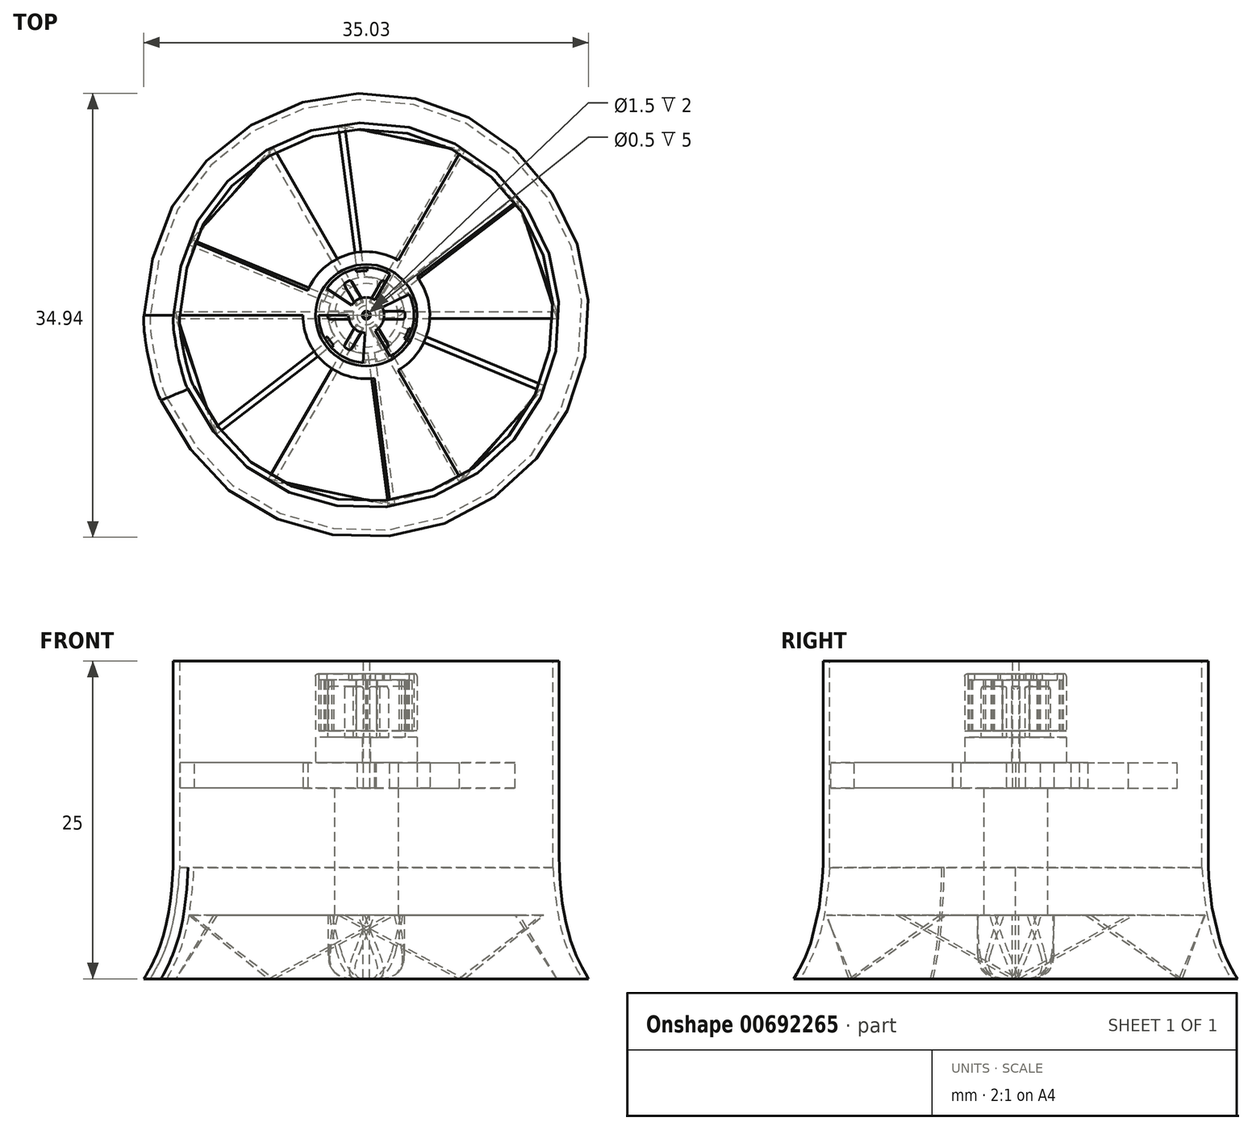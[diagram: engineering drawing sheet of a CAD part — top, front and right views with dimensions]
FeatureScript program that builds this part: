
annotation { "Feature Type Name" : "Feature", "Feature Type Description" : "" }
export const myFeature = defineFeature(function(context is Context, id is Id, definition is map)
    precondition{}
    {
        {
            var Q0;
            Q0=qCreatedBy(makeId("Top.planeOp"),FACE);
            var sketch = newSketch(context, id + "F0", { "sketchPlane" : qUnion([Q0])});
            skCircle(sketch, "E0", {"center": v(0, 0) * mm, "radius": 17.5 * mm});
            skCircle(sketch, "E1", {"center": v(0, 0) * mm, "radius": 15 * mm});
            skCircle(sketch, "E2", {"center": v(0, 0) * mm, "radius": 14.25 * mm});
            skCircle(sketch, "E3", {"center": v(0, 0) * mm, "radius": 0.5 * mm});
            skSolve(sketch);
        }
        {
            var Q0;
            Q0=qCreatedBy(makeId("Right.planeOp"),FACE);
            var sketch = newSketch(context, id + "F1", { "sketchPlane" : qUnion([Q0])});
            skFitSpline(sketch, "E4", {"points": [v(-17.47, 0) * mm, v(-16.4, 2.05) * mm, v(-15.16, 8.76) * mm], "startDerivative": vector(0.8, 0.84) * mm, "endDerivative": vector(0.72, 13.83) * mm});
            skLineSegment(sketch, "E5", {"start": v(-17.47, 0) * mm, "end": v(-16.97, 0) * mm});
            skLineSegment(sketch, "E6", {"start": v(0, 0) * mm, "end": v(0, 25) * mm});
            skLineSegment(sketch, "E7", {"start": v(-15.16, 8.76) * mm, "end": v(-15.16, 25) * mm});
            skLineSegment(sketch, "E8", {"start": v(-15.16, 25) * mm, "end": v(-14.66, 25) * mm});
            skLineSegment(sketch, "E9", {"start": v(-14.66, 25) * mm, "end": v(-14.66, 8.76) * mm});
            skLineSegment(sketch, "E10", {"start": v(-16.97, 0) * mm, "end": v(-17.47, 0) * mm});
            skFitSpline(sketch, "E11", {"points": [v(-16.97, 0) * mm, v(-15.9, 2.07) * mm, v(-14.66, 8.76) * mm], "startDerivative": vector(0.48, 0.72) * mm, "endDerivative": vector(0.94, 13.86) * mm});
            skLineSegment(sketch, "E12.MirrorCS", {"start": v(14.66, 25) * mm, "end": v(14.66, 8.76) * mm});
            skLineSegment(sketch, "E13.MirrorCS", {"start": v(15.16, 8.76) * mm, "end": v(15.16, 25) * mm});
            skLineSegment(sketch, "E14.MirrorCS", {"start": v(15.16, 25) * mm, "end": v(14.66, 25) * mm});
            skFitSpline(sketch, "E15.MirrorCS", {"points": [v(17.47, 0) * mm, v(16.4, 2.05) * mm, v(15.16, 8.76) * mm], "startDerivative": vector(-0.8, 0.84) * mm, "endDerivative": vector(-0.72, 13.83) * mm});
            skFitSpline(sketch, "E16.MirrorCS", {"points": [v(16.97, 0) * mm, v(15.9, 2.07) * mm, v(14.66, 8.76) * mm], "startDerivative": vector(-0.48, 0.72) * mm, "endDerivative": vector(-0.94, 13.86) * mm});
            skLineSegment(sketch, "E17.MirrorCS", {"start": v(16.97, 0) * mm, "end": v(17.47, 0) * mm});
            skSolve(sketch);
        }
        {
            var Q0;
            Q0=qCreatedBy(makeId("Front.planeOp"),FACE);
            var sketch = newSketch(context, id + "F2", { "sketchPlane" : qUnion([Q0])});
            skFitSpline(sketch, "E18", {"points": [v(-17.5, 0) * mm, v(-16.43, 2.05) * mm, v(-15.18, 8.76) * mm], "startDerivative": vector(0.8, 0.84) * mm, "endDerivative": vector(0.72, 13.83) * mm});
            skLineSegment(sketch, "E19", {"start": v(-15.18, 8.76) * mm, "end": v(-15.18, 25) * mm});
            skLineSegment(sketch, "E20", {"start": v(-15.18, 25) * mm, "end": v(-14.68, 25) * mm});
            skLineSegment(sketch, "E21", {"start": v(-14.68, 25) * mm, "end": v(-14.68, 8.76) * mm});
            skLineSegment(sketch, "E22", {"start": v(-17, 0) * mm, "end": v(-17.5, 0) * mm});
            skFitSpline(sketch, "E23", {"points": [v(-17, 0) * mm, v(-15.93, 2.07) * mm, v(-14.68, 8.76) * mm], "startDerivative": vector(0.48, 0.72) * mm, "endDerivative": vector(0.94, 13.86) * mm});
            skLineSegment(sketch, "E24.MirrorCS", {"start": v(14.68, 25) * mm, "end": v(14.68, 8.76) * mm});
            skLineSegment(sketch, "E25.MirrorCS", {"start": v(15.18, 8.76) * mm, "end": v(15.18, 25) * mm});
            skLineSegment(sketch, "E26.MirrorCS", {"start": v(15.18, 25) * mm, "end": v(14.68, 25) * mm});
            skFitSpline(sketch, "E27.MirrorCS", {"points": [v(17, 0) * mm, v(15.93, 2.07) * mm, v(14.68, 8.76) * mm], "startDerivative": vector(-0.48, 0.72) * mm, "endDerivative": vector(-0.94, 13.86) * mm});
            skFitSpline(sketch, "E28.MirrorCS", {"points": [v(17.5, 0) * mm, v(16.43, 2.05) * mm, v(15.18, 8.76) * mm], "startDerivative": vector(-0.8, 0.84) * mm, "endDerivative": vector(-0.72, 13.83) * mm});
            skLineSegment(sketch, "E29.MirrorCS", {"start": v(17, 0) * mm, "end": v(17.5, 0) * mm});
            skSolve(sketch);
        }
        {
            var Q0;
            Q0=qCreatedBy(makeId("Right.planeOp"),FACE);
            var Q1;
            Q1=qCreatedBy(makeId("Front.planeOp"),FACE);
            cPlane(context, id + "F3", {"entities" : qUnion([Q0, Q1]), "cplaneType" : CPlaneType.MID_PLANE, "offset" : 25 * mm, "width" : 150 * mm, "height" : 150 * mm});
        }
        {
            var Q0;
            Q0=qCreatedBy(makeId("Right.planeOp"),FACE);
            var Q1;
            Q1=qCreatedBy(makeId("Front.planeOp"),FACE);
            cPlane(context, id + "F4", {"entities" : qUnion([Q0, Q1]), "cplaneType" : CPlaneType.MID_PLANE, "offset" : 25 * mm, "flipAlignment" : true, "width" : 150 * mm, "height" : 150 * mm});
        }
        {
            var Q0;
            Q0=qCreatedBy(id+"F3.planeOp",FACE);
            var Q1;
            Q1=qCreatedBy(makeId("Right.planeOp"),FACE);
            cPlane(context, id + "F5", {"entities" : qUnion([Q0, Q1]), "cplaneType" : CPlaneType.MID_PLANE, "offset" : 25 * mm, "width" : 150 * mm, "height" : 150 * mm});
        }
        {
            var Q0;
            Q0=qCreatedBy(id+"F3.planeOp",FACE);
            var Q1;
            Q1=qCreatedBy(makeId("Right.planeOp"),FACE);
            cPlane(context, id + "F6", {"entities" : qUnion([Q0, Q1]), "cplaneType" : CPlaneType.MID_PLANE, "offset" : 25 * mm, "flipAlignment" : true, "width" : 150 * mm, "height" : 150 * mm});
        }
        {
            var Q0;
            Q0=qCreatedBy(makeId("Right.planeOp"),FACE);
            var Q1;
            Q1=qCreatedBy(id+"F4.planeOp",FACE);
            cPlane(context, id + "F7", {"entities" : qUnion([Q0, Q1]), "cplaneType" : CPlaneType.MID_PLANE, "offset" : 25 * mm, "width" : 150 * mm, "height" : 150 * mm});
        }
        {
            var Q0;
            Q0=qCreatedBy(makeId("Right.planeOp"),FACE);
            var Q1;
            Q1=qCreatedBy(id+"F4.planeOp",FACE);
            cPlane(context, id + "F8", {"entities" : qUnion([Q0, Q1]), "cplaneType" : CPlaneType.MID_PLANE, "offset" : 25 * mm, "flipAlignment" : true, "width" : 150 * mm, "height" : 150 * mm});
        }
        {
            var Q0;
            Q0=qCreatedBy(id+"F3.planeOp",FACE);
            var sketch = newSketch(context, id + "F9", { "sketchPlane" : qUnion([Q0])});
            skFitSpline(sketch, "E30", {"points": [v(-17.5, 0) * mm, v(-16.43, 2.05) * mm, v(-15.18, 8.76) * mm], "startDerivative": vector(0.8, 0.84) * mm, "endDerivative": vector(0.72, 13.83) * mm});
            skLineSegment(sketch, "E31", {"start": v(-15.18, 8.76) * mm, "end": v(-15.18, 25) * mm});
            skLineSegment(sketch, "E32", {"start": v(-15.18, 25) * mm, "end": v(-14.68, 25) * mm});
            skLineSegment(sketch, "E33", {"start": v(-14.68, 25) * mm, "end": v(-14.68, 8.76) * mm});
            skLineSegment(sketch, "E34", {"start": v(-17, 0) * mm, "end": v(-17.5, 0) * mm});
            skFitSpline(sketch, "E35", {"points": [v(-17, 0) * mm, v(-15.93, 2.07) * mm, v(-14.68, 8.76) * mm], "startDerivative": vector(0.48, 0.72) * mm, "endDerivative": vector(0.94, 13.86) * mm});
            skLineSegment(sketch, "E36.MirrorCS", {"start": v(14.68, 25) * mm, "end": v(14.68, 8.76) * mm});
            skLineSegment(sketch, "E37.MirrorCS", {"start": v(15.18, 8.76) * mm, "end": v(15.18, 25) * mm});
            skFitSpline(sketch, "E38.MirrorCS", {"points": [v(17, 0) * mm, v(15.93, 2.07) * mm, v(14.68, 8.76) * mm], "startDerivative": vector(-0.48, 0.72) * mm, "endDerivative": vector(-0.94, 13.86) * mm});
            skFitSpline(sketch, "E39.MirrorCS", {"points": [v(17.5, 0) * mm, v(16.43, 2.05) * mm, v(15.18, 8.76) * mm], "startDerivative": vector(-0.8, 0.84) * mm, "endDerivative": vector(-0.72, 13.83) * mm});
            skLineSegment(sketch, "E40.MirrorCS", {"start": v(15.18, 25) * mm, "end": v(14.68, 25) * mm});
            skLineSegment(sketch, "E41.MirrorCS", {"start": v(17, 0) * mm, "end": v(17.5, 0) * mm});
            skSolve(sketch);
        }
        {
            var Q0;
            Q0=qCreatedBy(id+"F4.planeOp",FACE);
            var sketch = newSketch(context, id + "F10", { "sketchPlane" : qUnion([Q0])});
            skFitSpline(sketch, "E42", {"points": [v(-17.5, 0) * mm, v(-16.43, 2.05) * mm, v(-15.18, 8.76) * mm], "startDerivative": vector(0.8, 0.84) * mm, "endDerivative": vector(0.72, 13.83) * mm});
            skLineSegment(sketch, "E43", {"start": v(-15.18, 8.76) * mm, "end": v(-15.18, 25) * mm});
            skLineSegment(sketch, "E44", {"start": v(-15.18, 25) * mm, "end": v(-14.68, 25) * mm});
            skLineSegment(sketch, "E45", {"start": v(-14.68, 25) * mm, "end": v(-14.68, 8.76) * mm});
            skLineSegment(sketch, "E46", {"start": v(-17, 0) * mm, "end": v(-17.5, 0) * mm});
            skFitSpline(sketch, "E47", {"points": [v(-17, 0) * mm, v(-15.93, 2.07) * mm, v(-14.68, 8.76) * mm], "startDerivative": vector(0.48, 0.72) * mm, "endDerivative": vector(0.94, 13.86) * mm});
            skLineSegment(sketch, "E48.MirrorCS", {"start": v(14.68, 25) * mm, "end": v(14.68, 8.76) * mm});
            skLineSegment(sketch, "E49.MirrorCS", {"start": v(15.18, 8.76) * mm, "end": v(15.18, 25) * mm});
            skLineSegment(sketch, "E50.MirrorCS", {"start": v(15.18, 25) * mm, "end": v(14.68, 25) * mm});
            skFitSpline(sketch, "E51.MirrorCS", {"points": [v(17.5, 0) * mm, v(16.43, 2.05) * mm, v(15.18, 8.76) * mm], "startDerivative": vector(-0.8, 0.84) * mm, "endDerivative": vector(-0.72, 13.83) * mm});
            skFitSpline(sketch, "E52.MirrorCS", {"points": [v(17, 0) * mm, v(15.93, 2.07) * mm, v(14.68, 8.76) * mm], "startDerivative": vector(-0.48, 0.72) * mm, "endDerivative": vector(-0.94, 13.86) * mm});
            skLineSegment(sketch, "E53.MirrorCS", {"start": v(17, 0) * mm, "end": v(17.5, 0) * mm});
            skSolve(sketch);
        }
        {
            var Q0;
            Q0=qCreatedBy(id+"F5.planeOp",FACE);
            var sketch = newSketch(context, id + "F11", { "sketchPlane" : qUnion([Q0])});
            skFitSpline(sketch, "E54", {"points": [v(-17.5, 0) * mm, v(-16.43, 2.05) * mm, v(-15.18, 8.76) * mm], "startDerivative": vector(0.8, 0.84) * mm, "endDerivative": vector(0.72, 13.83) * mm});
            skLineSegment(sketch, "E55", {"start": v(-15.18, 8.76) * mm, "end": v(-15.18, 25) * mm});
            skLineSegment(sketch, "E56", {"start": v(-15.18, 25) * mm, "end": v(-14.68, 25) * mm});
            skLineSegment(sketch, "E57", {"start": v(-14.68, 25) * mm, "end": v(-14.68, 8.76) * mm});
            skLineSegment(sketch, "E58", {"start": v(-17, 0) * mm, "end": v(-17.5, 0) * mm});
            skFitSpline(sketch, "E59", {"points": [v(-17, 0) * mm, v(-15.93, 2.07) * mm, v(-14.68, 8.76) * mm], "startDerivative": vector(0.48, 0.72) * mm, "endDerivative": vector(0.94, 13.86) * mm});
            skLineSegment(sketch, "E60.MirrorCS", {"start": v(14.68, 25) * mm, "end": v(14.68, 8.76) * mm});
            skLineSegment(sketch, "E61.MirrorCS", {"start": v(15.18, 25) * mm, "end": v(14.68, 25) * mm});
            skLineSegment(sketch, "E62.MirrorCS", {"start": v(15.18, 8.76) * mm, "end": v(15.18, 25) * mm});
            skFitSpline(sketch, "E63.MirrorCS", {"points": [v(17, 0) * mm, v(15.93, 2.07) * mm, v(14.68, 8.76) * mm], "startDerivative": vector(-0.48, 0.72) * mm, "endDerivative": vector(-0.94, 13.86) * mm});
            skFitSpline(sketch, "E64.MirrorCS", {"points": [v(17.5, 0) * mm, v(16.43, 2.05) * mm, v(15.18, 8.76) * mm], "startDerivative": vector(-0.8, 0.84) * mm, "endDerivative": vector(-0.72, 13.83) * mm});
            skLineSegment(sketch, "E65.MirrorCS", {"start": v(17, 0) * mm, "end": v(17.5, 0) * mm});
            skSolve(sketch);
        }
        {
            var Q0;
            Q0=qCreatedBy(id+"F6.planeOp",FACE);
            var sketch = newSketch(context, id + "F12", { "sketchPlane" : qUnion([Q0])});
            skFitSpline(sketch, "E66", {"points": [v(-17.5, 0) * mm, v(-16.43, 2.05) * mm, v(-15.18, 8.76) * mm], "startDerivative": vector(0.8, 0.84) * mm, "endDerivative": vector(0.72, 13.83) * mm});
            skLineSegment(sketch, "E67", {"start": v(-15.18, 8.76) * mm, "end": v(-15.18, 25) * mm});
            skLineSegment(sketch, "E68", {"start": v(-15.18, 25) * mm, "end": v(-14.68, 25) * mm});
            skLineSegment(sketch, "E69", {"start": v(-14.68, 25) * mm, "end": v(-14.68, 8.76) * mm});
            skLineSegment(sketch, "E70", {"start": v(-17, 0) * mm, "end": v(-17.5, 0) * mm});
            skFitSpline(sketch, "E71", {"points": [v(-17, 0) * mm, v(-15.93, 2.07) * mm, v(-14.68, 8.76) * mm], "startDerivative": vector(0.48, 0.72) * mm, "endDerivative": vector(0.94, 13.86) * mm});
            skLineSegment(sketch, "E72.MirrorCS", {"start": v(14.68, 25) * mm, "end": v(14.68, 8.76) * mm});
            skLineSegment(sketch, "E73.MirrorCS", {"start": v(15.18, 8.76) * mm, "end": v(15.18, 25) * mm});
            skFitSpline(sketch, "E74.MirrorCS", {"points": [v(17, 0) * mm, v(15.93, 2.07) * mm, v(14.68, 8.76) * mm], "startDerivative": vector(-0.48, 0.72) * mm, "endDerivative": vector(-0.94, 13.86) * mm});
            skFitSpline(sketch, "E75.MirrorCS", {"points": [v(17.5, 0) * mm, v(16.43, 2.05) * mm, v(15.18, 8.76) * mm], "startDerivative": vector(-0.8, 0.84) * mm, "endDerivative": vector(-0.72, 13.83) * mm});
            skLineSegment(sketch, "E76.MirrorCS", {"start": v(15.18, 25) * mm, "end": v(14.68, 25) * mm});
            skLineSegment(sketch, "E77.MirrorCS", {"start": v(17, 0) * mm, "end": v(17.5, 0) * mm});
            skSolve(sketch);
        }
        {
            var Q0;
            Q0=qCreatedBy(id+"F7.planeOp",FACE);
            var sketch = newSketch(context, id + "F13", { "sketchPlane" : qUnion([Q0])});
            skFitSpline(sketch, "E78", {"points": [v(-17.5, 0) * mm, v(-16.43, 2.05) * mm, v(-15.18, 8.76) * mm], "startDerivative": vector(0.8, 0.84) * mm, "endDerivative": vector(0.72, 13.83) * mm});
            skLineSegment(sketch, "E79", {"start": v(-15.18, 8.76) * mm, "end": v(-15.18, 25) * mm});
            skLineSegment(sketch, "E80", {"start": v(-15.18, 25) * mm, "end": v(-14.68, 25) * mm});
            skLineSegment(sketch, "E81", {"start": v(-14.68, 25) * mm, "end": v(-14.68, 8.76) * mm});
            skLineSegment(sketch, "E82", {"start": v(-17, 0) * mm, "end": v(-17.5, 0) * mm});
            skFitSpline(sketch, "E83", {"points": [v(-17, 0) * mm, v(-15.93, 2.07) * mm, v(-14.68, 8.76) * mm], "startDerivative": vector(0.48, 0.72) * mm, "endDerivative": vector(0.94, 13.86) * mm});
            skLineSegment(sketch, "E84.MirrorCS", {"start": v(14.68, 25) * mm, "end": v(14.68, 8.76) * mm});
            skLineSegment(sketch, "E85.MirrorCS", {"start": v(15.18, 8.76) * mm, "end": v(15.18, 25) * mm});
            skFitSpline(sketch, "E86.MirrorCS", {"points": [v(17, 0) * mm, v(15.93, 2.07) * mm, v(14.68, 8.76) * mm], "startDerivative": vector(-0.48, 0.72) * mm, "endDerivative": vector(-0.94, 13.86) * mm});
            skFitSpline(sketch, "E87.MirrorCS", {"points": [v(17.5, 0) * mm, v(16.43, 2.05) * mm, v(15.18, 8.76) * mm], "startDerivative": vector(-0.8, 0.84) * mm, "endDerivative": vector(-0.72, 13.83) * mm});
            skLineSegment(sketch, "E88.MirrorCS", {"start": v(15.18, 25) * mm, "end": v(14.68, 25) * mm});
            skLineSegment(sketch, "E89.MirrorCS", {"start": v(17, 0) * mm, "end": v(17.5, 0) * mm});
            skSolve(sketch);
        }
        {
            var Q0;
            Q0=qCreatedBy(id+"F8.planeOp",FACE);
            var sketch = newSketch(context, id + "F14", { "sketchPlane" : qUnion([Q0])});
            skFitSpline(sketch, "E90", {"points": [v(-17.5, 0) * mm, v(-16.43, 2.05) * mm, v(-15.18, 8.76) * mm], "startDerivative": vector(0.8, 0.84) * mm, "endDerivative": vector(0.72, 13.83) * mm});
            skLineSegment(sketch, "E91", {"start": v(-15.18, 8.76) * mm, "end": v(-15.18, 25) * mm});
            skLineSegment(sketch, "E92", {"start": v(-15.18, 25) * mm, "end": v(-14.68, 25) * mm});
            skLineSegment(sketch, "E93", {"start": v(-14.68, 25) * mm, "end": v(-14.68, 8.76) * mm});
            skLineSegment(sketch, "E94", {"start": v(-17, 0) * mm, "end": v(-17.5, 0) * mm});
            skFitSpline(sketch, "E95", {"points": [v(-17, 0) * mm, v(-15.93, 2.07) * mm, v(-14.68, 8.76) * mm], "startDerivative": vector(0.48, 0.72) * mm, "endDerivative": vector(0.94, 13.86) * mm});
            skLineSegment(sketch, "E96.MirrorCS", {"start": v(14.68, 25) * mm, "end": v(14.68, 8.76) * mm});
            skLineSegment(sketch, "E97.MirrorCS", {"start": v(15.18, 8.76) * mm, "end": v(15.18, 25) * mm});
            skFitSpline(sketch, "E98.MirrorCS", {"points": [v(17.5, 0) * mm, v(16.43, 2.05) * mm, v(15.18, 8.76) * mm], "startDerivative": vector(-0.8, 0.84) * mm, "endDerivative": vector(-0.72, 13.83) * mm});
            skFitSpline(sketch, "E99.MirrorCS", {"points": [v(17, 0) * mm, v(15.93, 2.07) * mm, v(14.68, 8.76) * mm], "startDerivative": vector(-0.48, 0.72) * mm, "endDerivative": vector(-0.94, 13.86) * mm});
            skLineSegment(sketch, "E100.MirrorCS", {"start": v(17, 0) * mm, "end": v(17.5, 0) * mm});
            skLineSegment(sketch, "E101.MirrorCS", {"start": v(15.18, 25) * mm, "end": v(14.68, 25) * mm});
            skSolve(sketch);
        }
        {
            var Q0;
            Q0=makeQuery(id+"F11.imprint","IMPRINT",FACE,{"disambiguationData":[TD([[makeQuery(id+"F11.imprint","IMPRINT",EDGE,{"derivedFrom":sQuery(id+"F11.wireOp",EDGE,"E60.MirrorCS")}),1.0]])]});
            var Q1;
            Q1=makeQuery(id+"F10.imprint","IMPRINT",FACE,{"disambiguationData":[TD([[makeQuery(id+"F10.imprint","IMPRINT",EDGE,{"derivedFrom":sQuery(id+"F10.wireOp",EDGE,"E42")}),-1.0]])]});
            var Q2;
            Q2=makeQuery(id+"F14.imprint","IMPRINT",FACE,{"disambiguationData":[TD([[makeQuery(id+"F14.imprint","IMPRINT",EDGE,{"derivedFrom":sQuery(id+"F14.wireOp",EDGE,"E90")}),-1.0]])]});
            var Q3;
            Q3=makeQuery(id+"F1.imprint","IMPRINT",FACE,{"disambiguationData":[TD([[makeQuery(id+"F1.imprint","IMPRINT",EDGE,{"derivedFrom":sQuery(id+"F1.wireOp",EDGE,"E4")}),-1.0]])]});
            var Q4;
            Q4=makeQuery(id+"F12.imprint","IMPRINT",FACE,{"disambiguationData":[TD([[makeQuery(id+"F12.imprint","IMPRINT",EDGE,{"derivedFrom":sQuery(id+"F12.wireOp",EDGE,"E66")}),-1.0]])]});
            var Q5;
            Q5=makeQuery(id+"F9.imprint","IMPRINT",FACE,{"disambiguationData":[TD([[makeQuery(id+"F9.imprint","IMPRINT",EDGE,{"derivedFrom":sQuery(id+"F9.wireOp",EDGE,"E30")}),-1.0]])]});
            var Q6;
            Q6=makeQuery(id+"F13.imprint","IMPRINT",FACE,{"disambiguationData":[TD([[makeQuery(id+"F13.imprint","IMPRINT",EDGE,{"derivedFrom":sQuery(id+"F13.wireOp",EDGE,"E78")}),-1.0]])]});
            var Q7;
            Q7=makeQuery(id+"F2.imprint","IMPRINT",FACE,{"disambiguationData":[TD([[makeQuery(id+"F2.imprint","IMPRINT",EDGE,{"derivedFrom":sQuery(id+"F2.wireOp",EDGE,"E24.MirrorCS")}),1.0]])]});
            var Q8;
            Q8=makeQuery(id+"F11.imprint","IMPRINT",FACE,{"disambiguationData":[TD([[makeQuery(id+"F11.imprint","IMPRINT",EDGE,{"derivedFrom":sQuery(id+"F11.wireOp",EDGE,"E54")}),-1.0]])]});
            var Q9;
            Q9=makeQuery(id+"F10.imprint","IMPRINT",FACE,{"disambiguationData":[TD([[makeQuery(id+"F10.imprint","IMPRINT",EDGE,{"derivedFrom":sQuery(id+"F10.wireOp",EDGE,"E48.MirrorCS")}),1.0]])]});
            var Q10;
            Q10=makeQuery(id+"F14.imprint","IMPRINT",FACE,{"disambiguationData":[TD([[makeQuery(id+"F14.imprint","IMPRINT",EDGE,{"derivedFrom":sQuery(id+"F14.wireOp",EDGE,"E96.MirrorCS")}),1.0]])]});
            var Q11;
            Q11=makeQuery(id+"F1.imprint","IMPRINT",FACE,{"disambiguationData":[TD([[makeQuery(id+"F1.imprint","IMPRINT",EDGE,{"derivedFrom":sQuery(id+"F1.wireOp",EDGE,"E12.MirrorCS")}),1.0]])]});
            var Q12;
            Q12=makeQuery(id+"F12.imprint","IMPRINT",FACE,{"disambiguationData":[TD([[makeQuery(id+"F12.imprint","IMPRINT",EDGE,{"derivedFrom":sQuery(id+"F12.wireOp",EDGE,"E72.MirrorCS")}),1.0]])]});
            var Q13;
            Q13=makeQuery(id+"F9.imprint","IMPRINT",FACE,{"disambiguationData":[TD([[makeQuery(id+"F9.imprint","IMPRINT",EDGE,{"derivedFrom":sQuery(id+"F9.wireOp",EDGE,"E36.MirrorCS")}),1.0]])]});
            var Q14;
            Q14=makeQuery(id+"F13.imprint","IMPRINT",FACE,{"disambiguationData":[TD([[makeQuery(id+"F13.imprint","IMPRINT",EDGE,{"derivedFrom":sQuery(id+"F13.wireOp",EDGE,"E84.MirrorCS")}),1.0]])]});
            var Q15;
            Q15=makeQuery(id+"F2.imprint","IMPRINT",FACE,{"disambiguationData":[TD([[makeQuery(id+"F2.imprint","IMPRINT",EDGE,{"derivedFrom":sQuery(id+"F2.wireOp",EDGE,"E18")}),-1.0]])]});
            loft(context, id + "F15", {"sheetProfilesArray" : [{ "sheetProfileEntities" : qUnion([Q0]) }, { "sheetProfileEntities" : qUnion([Q1]) }, { "sheetProfileEntities" : qUnion([Q2]) }, { "sheetProfileEntities" : qUnion([Q3]) }, { "sheetProfileEntities" : qUnion([Q4]) }, { "sheetProfileEntities" : qUnion([Q5]) }, { "sheetProfileEntities" : qUnion([Q6]) }, { "sheetProfileEntities" : qUnion([Q7]) }, { "sheetProfileEntities" : qUnion([Q8]) }, { "sheetProfileEntities" : qUnion([Q9]) }, { "sheetProfileEntities" : qUnion([Q10]) }, { "sheetProfileEntities" : qUnion([Q11]) }, { "sheetProfileEntities" : qUnion([Q12]) }, { "sheetProfileEntities" : qUnion([Q13]) }, { "sheetProfileEntities" : qUnion([Q14]) }, { "sheetProfileEntities" : qUnion([Q15]) }]});
        }
        {
            var Q1;
            Q1=makeQuery(id+"F15.opLoft","CAP_FACE",FACE,{"disambiguationData":[OSD([makeQuery(id+"F2.imprint","IMPRINT",FACE,{"disambiguationData":[TD([[makeQuery(id+"F2.imprint","IMPRINT",EDGE,{"derivedFrom":sQuery(id+"F2.wireOp",EDGE,"E18")}),-1.0]])]})])],"isStart":true});
            var Q2;
            Q2=makeQuery(id+"F15.opLoft","CAP_FACE",FACE,{"disambiguationData":[OSD([makeQuery(id+"F11.imprint","IMPRINT",FACE,{"disambiguationData":[TD([[makeQuery(id+"F11.imprint","IMPRINT",EDGE,{"derivedFrom":sQuery(id+"F11.wireOp",EDGE,"E60.MirrorCS")}),1.0]])]})])],"isStart":true});
            loft(context, id + "F16", {"operationType" : NewBodyOperationType.ADD, "startCondition" : LoftEndDerivativeType.MATCH_CURVATURE, "startMagnitude" : 0.5, "endCondition" : LoftEndDerivativeType.MATCH_CURVATURE, "endMagnitude" : 0.5, "sheetProfilesArray" : [{ "sheetProfileEntities" : qUnion([Q1]) }, { "sheetProfileEntities" : qUnion([Q2]) }]});
        }
        {
            var Q0;
            Q0=qCreatedBy(makeId("Top.planeOp"),FACE);
            cPlane(context, id + "F17", {"entities" : qUnion([Q0]), "cplaneType" : CPlaneType.OFFSET, "offset" : 15 * mm, "width" : 150 * mm, "height" : 150 * mm});
        }
        {
            var Q0;
            Q0=qCreatedBy(id+"F17.planeOp",FACE);
            var sketch = newSketch(context, id + "F18", { "sketchPlane" : qUnion([Q0])});
            skCircle(sketch, "E102", {"center": v(0, 0) * mm, "radius": 5 * mm});
            skArc(sketch, "E103", {"start": v(-13.6, 5.72) * mm, "mid": v(-14.46, 2.92) * mm, "end": v(-14.75, 0) * mm});
            skLineSegment(sketch, "E104", {"start": v(-5, 0) * mm, "end": v(-14.75, 0) * mm});
            skLineSegment(sketch, "E105", {"start": v(-4.6, 1.94) * mm, "end": v(-13.6, 5.72) * mm});
            skLineSegment(sketch, "E106.1.0", {"start": v(2.5, -4.33) * mm, "end": v(7.38, -12.77) * mm});
            skLineSegment(sketch, "E106.1.1", {"start": v(0.62, -4.96) * mm, "end": v(1.84, -14.63) * mm});
            skArc(sketch, "E106.1.2", {"start": v(1.84, -14.63) * mm, "mid": v(4.7, -13.98) * mm, "end": v(7.37, -12.77) * mm});
            skLineSegment(sketch, "E106.2.0", {"start": v(2.5, 4.33) * mm, "end": v(7.38, 12.77) * mm});
            skLineSegment(sketch, "E106.2.1", {"start": v(3.98, 3.02) * mm, "end": v(11.75, 8.91) * mm});
            skArc(sketch, "E106.2.2", {"start": v(11.75, 8.91) * mm, "mid": v(9.76, 11.06) * mm, "end": v(7.38, 12.77) * mm});
            skCircle(sketch, "E107", {"center": v(0, 0) * mm, "radius": 0.75 * mm});
            skSolve(sketch);
        }
        {
            var Q0;
            {var subQ0=sQuery(id+"F18.wireOp",EDGE,"E106.2.0");Q0=makeQuery(id+"F18.imprint","IMPRINT",FACE,{"disambiguationData":[TD([[makeQuery(id+"F18.imprint","IMPRINT",EDGE,{"derivedFrom":subQ0}),-1.0]])]});}
            var Q1;
            Q1=makeQuery(id+"F18.imprint","IMPRINT",FACE,{"disambiguationData":[TD([[makeQuery(id+"F18.imprint","IMPRINT",EDGE,{"derivedFrom":sQuery(id+"F18.wireOp",EDGE,"E103")}),1.0]])]});
            var Q2;
            {var subQ0=sQuery(id+"F18.wireOp",EDGE,"E102");var subQ4=makeQuery(id+"F18.imprint","INTERSECT",VERTEX,{"derivedFrom":[subQ0,sQuery(id+"F18.wireOp",EDGE,"E106.2.0")]});Q2=makeQuery(id+"F18.imprint","IMPRINT",FACE,{"disambiguationData":[TD([[makeQuery(id+"F18.imprint","IMPRINT",EDGE,{"disambiguationData":[TD([[subQ4,1.0]])],"derivedFrom":subQ0}),1.0]])]});}
            var Q3;
            {var subQ0=sQuery(id+"F18.wireOp",EDGE,"E106.1.0");Q3=makeQuery(id+"F18.imprint","IMPRINT",FACE,{"disambiguationData":[TD([[makeQuery(id+"F18.imprint","IMPRINT",EDGE,{"derivedFrom":subQ0}),-1.0]])]});}
            extrude(context, id + "F19", {"entities" : qUnion([Q0, Q1, Q2, Q3]), "operationType" : NewBodyOperationType.ADD, "depth" : 2 * mm, "offsetDistance" : 25 * mm});
        }
        {
            var Q0;
            Q0=qCreatedBy(makeId("Top.planeOp"),FACE);
            cPlane(context, id + "F20", {"entities" : qUnion([Q0]), "cplaneType" : CPlaneType.OFFSET, "offset" : 5 * mm, "width" : 150 * mm, "height" : 150 * mm});
        }
        {
            var Q0;
            Q0=qCreatedBy(id+"F20.planeOp",FACE);
            var sketch = newSketch(context, id + "F21", { "sketchPlane" : qUnion([Q0])});
            skCircle(sketch, "E108", {"center": v(0, 0) * mm, "radius": 3 * mm});
            skCircle(sketch, "E109", {"center": v(0, 0) * mm, "radius": 15 * mm});
            skCircle(sketch, "E110", {"center": v(0, 0) * mm, "radius": 0.25 * mm});
            skSolve(sketch);
        }
        {
            var Q0;
            Q0=makeQuery(id+"F21.imprint","IMPRINT",FACE,{"disambiguationData":[TD([[makeQuery(id+"F21.imprint","IMPRINT",EDGE,{"derivedFrom":sQuery(id+"F21.wireOp",EDGE,"E108")}),1.0]])]});
            extrude(context, id + "F22", {"entities" : qUnion([Q0]), "oppositeDirection" : true, "depth" : 5 * mm, "offsetDistance" : 25 * mm});
        }
        {
            var Q0;
            Q0=makeQuery(id+"F22.opExtrude","CAP_EDGE",EDGE,{"disambiguationData":[OSD([sQuery(id+"F21.wireOp",EDGE,"E108")])],"isStart":false});
            fillet(context, id + "F23", {"entities" : qUnion([Q0]), "radius" : 2 * mm, "rho" : 0.5, "crossSection" : FilletCrossSection.CONIC, "allowEdgeOverflow" : false});
        }
        {
            var Q0;
            Q0=qCreatedBy(makeId("Top.planeOp"),FACE);
            var sketch = newSketch(context, id + "F24", { "sketchPlane" : qUnion([Q0])});
            skLineSegment(sketch, "E111", {"start": v(0, 0.25) * mm, "end": v(0, -0.25) * mm});
            skLineSegment(sketch, "E112", {"start": v(-0.43, 0.25) * mm, "end": v(-15, 0.25) * mm});
            skLineSegment(sketch, "E113", {"start": v(-15, 0.25) * mm, "end": v(-15, -0.25) * mm});
            skLineSegment(sketch, "E114", {"start": v(-15, -0.25) * mm, "end": v(-0.43, -0.25) * mm});
            skArc(sketch, "E115", {"start": v(-0.43, 0.25) * mm, "mid": v(-0.5, 0) * mm, "end": v(-0.43, -0.25) * mm});
            skLineSegment(sketch, "E116.1.0", {"start": v(-7.72, -12.87) * mm, "end": v(-7.28, -13.12) * mm});
            skLineSegment(sketch, "E116.1.1", {"start": v(-0.43, -0.25) * mm, "end": v(-7.72, -12.87) * mm});
            skLineSegment(sketch, "E116.1.2", {"start": v(-7.28, -13.12) * mm, "end": v(0, -0.5) * mm});
            skArc(sketch, "E116.1.3", {"start": v(-0.43, -0.25) * mm, "mid": v(-0.25, -0.43) * mm, "end": v(0, -0.5) * mm});
            skLineSegment(sketch, "E116.2.0", {"start": v(7.28, -13.12) * mm, "end": v(7.72, -12.87) * mm});
            skLineSegment(sketch, "E116.2.1", {"start": v(0, -0.5) * mm, "end": v(7.28, -13.12) * mm});
            skLineSegment(sketch, "E116.2.2", {"start": v(7.72, -12.87) * mm, "end": v(0.43, -0.25) * mm});
            skArc(sketch, "E116.2.3", {"start": v(0, -0.5) * mm, "mid": v(0.25, -0.43) * mm, "end": v(0.43, -0.25) * mm});
            skLineSegment(sketch, "E116.3.0", {"start": v(15, -0.25) * mm, "end": v(15, 0.25) * mm});
            skLineSegment(sketch, "E116.3.1", {"start": v(0.43, -0.25) * mm, "end": v(15, -0.25) * mm});
            skLineSegment(sketch, "E116.3.2", {"start": v(15, 0.25) * mm, "end": v(0.43, 0.25) * mm});
            skArc(sketch, "E116.3.3", {"start": v(0.43, -0.25) * mm, "mid": v(0.5, 0) * mm, "end": v(0.43, 0.25) * mm});
            skLineSegment(sketch, "E116.4.0", {"start": v(7.72, 12.87) * mm, "end": v(7.28, 13.12) * mm});
            skLineSegment(sketch, "E116.4.1", {"start": v(0.43, 0.25) * mm, "end": v(7.72, 12.87) * mm});
            skLineSegment(sketch, "E116.4.2", {"start": v(7.28, 13.12) * mm, "end": v(0, 0.5) * mm});
            skArc(sketch, "E116.4.3", {"start": v(0.43, 0.25) * mm, "mid": v(0.25, 0.43) * mm, "end": v(0, 0.5) * mm});
            skLineSegment(sketch, "E116.5.0", {"start": v(-7.28, 13.12) * mm, "end": v(-7.72, 12.87) * mm});
            skLineSegment(sketch, "E116.5.1", {"start": v(0, 0.5) * mm, "end": v(-7.28, 13.12) * mm});
            skLineSegment(sketch, "E116.5.2", {"start": v(-7.72, 12.87) * mm, "end": v(-0.43, 0.25) * mm});
            skArc(sketch, "E116.5.3", {"start": v(0, 0.5) * mm, "mid": v(-0.25, 0.43) * mm, "end": v(-0.43, 0.25) * mm});
            skSolve(sketch);
        }
        {
            var Q0;
            Q0=qCreatedBy(id+"F20.planeOp",FACE);
            var sketch = newSketch(context, id + "F25", { "sketchPlane" : qUnion([Q0])});
            skLineSegment(sketch, "E117", {"start": v(-0.5, -0.07) * mm, "end": v(-13.95, 5.5) * mm});
            skLineSegment(sketch, "E118", {"start": v(-13.95, 5.5) * mm, "end": v(-13.76, 5.97) * mm});
            skLineSegment(sketch, "E119", {"start": v(-13.76, 5.97) * mm, "end": v(-0.3, 0.4) * mm});
            skArc(sketch, "E120", {"start": v(-0.3, 0.4) * mm, "mid": v(-0.46, 0.2) * mm, "end": v(-0.5, -0.07) * mm});
            skLineSegment(sketch, "E121.1.0", {"start": v(-12.05, -8.93) * mm, "end": v(-0.5, -0.07) * mm});
            skLineSegment(sketch, "E121.1.1", {"start": v(-0.2, -0.46) * mm, "end": v(-11.75, -9.33) * mm});
            skLineSegment(sketch, "E121.1.2", {"start": v(-11.75, -9.33) * mm, "end": v(-12.05, -8.93) * mm});
            skArc(sketch, "E121.1.3", {"start": v(-0.5, -0.07) * mm, "mid": v(-0.4, -0.3) * mm, "end": v(-0.2, -0.46) * mm});
            skLineSegment(sketch, "E121.2.0", {"start": v(1.71, -14.9) * mm, "end": v(-0.2, -0.46) * mm});
            skLineSegment(sketch, "E121.2.1", {"start": v(0.3, -0.4) * mm, "end": v(2.2, -14.84) * mm});
            skLineSegment(sketch, "E121.2.2", {"start": v(2.2, -14.84) * mm, "end": v(1.71, -14.9) * mm});
            skArc(sketch, "E121.2.3", {"start": v(-0.2, -0.46) * mm, "mid": v(0.07, -0.5) * mm, "end": v(0.3, -0.4) * mm});
            skLineSegment(sketch, "E121.3.0", {"start": v(13.76, -5.97) * mm, "end": v(0.3, -0.4) * mm});
            skLineSegment(sketch, "E121.3.1", {"start": v(0.5, 0.07) * mm, "end": v(13.95, -5.5) * mm});
            skLineSegment(sketch, "E121.3.2", {"start": v(13.95, -5.5) * mm, "end": v(13.76, -5.97) * mm});
            skArc(sketch, "E121.3.3", {"start": v(0.3, -0.4) * mm, "mid": v(0.46, -0.2) * mm, "end": v(0.5, 0.07) * mm});
            skLineSegment(sketch, "E121.4.0", {"start": v(12.05, 8.93) * mm, "end": v(0.5, 0.07) * mm});
            skLineSegment(sketch, "E121.4.1", {"start": v(0.2, 0.46) * mm, "end": v(11.75, 9.33) * mm});
            skLineSegment(sketch, "E121.4.2", {"start": v(11.75, 9.33) * mm, "end": v(12.05, 8.93) * mm});
            skArc(sketch, "E121.4.3", {"start": v(0.5, 0.07) * mm, "mid": v(0.4, 0.3) * mm, "end": v(0.2, 0.46) * mm});
            skLineSegment(sketch, "E121.5.0", {"start": v(-1.71, 14.9) * mm, "end": v(0.2, 0.46) * mm});
            skLineSegment(sketch, "E121.5.1", {"start": v(-0.3, 0.4) * mm, "end": v(-2.2, 14.84) * mm});
            skLineSegment(sketch, "E121.5.2", {"start": v(-2.2, 14.84) * mm, "end": v(-1.71, 14.9) * mm});
            skArc(sketch, "E121.5.3", {"start": v(0.2, 0.46) * mm, "mid": v(-0.07, 0.5) * mm, "end": v(-0.3, 0.4) * mm});
            skSolve(sketch);
        }
        {
            var Q1;
            Q1=makeQuery(id+"F24.imprint","IMPRINT",FACE,{"disambiguationData":[TD([[makeQuery(id+"F24.imprint","IMPRINT",EDGE,{"derivedFrom":sQuery(id+"F24.wireOp",EDGE,"E116.1.0")}),1.0]])]});
            var Q2;
            Q2=makeQuery(id+"F25.imprint","IMPRINT",FACE,{"disambiguationData":[TD([[makeQuery(id+"F25.imprint","IMPRINT",EDGE,{"derivedFrom":sQuery(id+"F25.wireOp",EDGE,"E121.2.0")}),-1.0]])]});
            loft(context, id + "F26", {"operationType" : NewBodyOperationType.ADD, "sheetProfilesArray" : [{ "sheetProfileEntities" : qUnion([Q1]) }, { "sheetProfileEntities" : qUnion([Q2]) }]});
        }
        {
            var Q1;
            Q1=makeQuery(id+"F24.imprint","IMPRINT",FACE,{"disambiguationData":[TD([[makeQuery(id+"F24.imprint","IMPRINT",EDGE,{"derivedFrom":sQuery(id+"F24.wireOp",EDGE,"E116.2.0")}),1.0]])]});
            var Q2;
            Q2=makeQuery(id+"F25.imprint","IMPRINT",FACE,{"disambiguationData":[TD([[makeQuery(id+"F25.imprint","IMPRINT",EDGE,{"derivedFrom":sQuery(id+"F25.wireOp",EDGE,"E121.3.0")}),-1.0]])]});
            loft(context, id + "F27", {"operationType" : NewBodyOperationType.ADD, "sheetProfilesArray" : [{ "sheetProfileEntities" : qUnion([Q1]) }, { "sheetProfileEntities" : qUnion([Q2]) }]});
        }
        {
            var Q1;
            Q1=makeQuery(id+"F24.imprint","IMPRINT",FACE,{"disambiguationData":[TD([[makeQuery(id+"F24.imprint","IMPRINT",EDGE,{"derivedFrom":sQuery(id+"F24.wireOp",EDGE,"E116.3.0")}),1.0]])]});
            var Q2;
            Q2=makeQuery(id+"F25.imprint","IMPRINT",FACE,{"disambiguationData":[TD([[makeQuery(id+"F25.imprint","IMPRINT",EDGE,{"derivedFrom":sQuery(id+"F25.wireOp",EDGE,"E121.4.0")}),-1.0]])]});
            loft(context, id + "F28", {"operationType" : NewBodyOperationType.ADD, "sheetProfilesArray" : [{ "sheetProfileEntities" : qUnion([Q1]) }, { "sheetProfileEntities" : qUnion([Q2]) }]});
        }
        {
            var Q1;
            Q1=makeQuery(id+"F25.imprint","IMPRINT",FACE,{"disambiguationData":[TD([[makeQuery(id+"F25.imprint","IMPRINT",EDGE,{"derivedFrom":sQuery(id+"F25.wireOp",EDGE,"E121.5.0")}),-1.0]])]});
            var Q2;
            Q2=makeQuery(id+"F24.imprint","IMPRINT",FACE,{"disambiguationData":[TD([[makeQuery(id+"F24.imprint","IMPRINT",EDGE,{"derivedFrom":sQuery(id+"F24.wireOp",EDGE,"E116.4.0")}),1.0]])]});
            loft(context, id + "F29", {"operationType" : NewBodyOperationType.ADD, "sheetProfilesArray" : [{ "sheetProfileEntities" : qUnion([Q1]) }, { "sheetProfileEntities" : qUnion([Q2]) }]});
        }
        {
            var Q1;
            Q1=makeQuery(id+"F25.imprint","IMPRINT",FACE,{"disambiguationData":[TD([[makeQuery(id+"F25.imprint","IMPRINT",EDGE,{"derivedFrom":sQuery(id+"F25.wireOp",EDGE,"E117")}),-1.0]])]});
            var Q2;
            Q2=makeQuery(id+"F24.imprint","IMPRINT",FACE,{"disambiguationData":[TD([[makeQuery(id+"F24.imprint","IMPRINT",EDGE,{"derivedFrom":sQuery(id+"F24.wireOp",EDGE,"E116.5.0")}),1.0]])]});
            loft(context, id + "F30", {"operationType" : NewBodyOperationType.ADD, "sheetProfilesArray" : [{ "sheetProfileEntities" : qUnion([Q1]) }, { "sheetProfileEntities" : qUnion([Q2]) }]});
        }
        {
            var Q1;
            Q1=makeQuery(id+"F25.imprint","IMPRINT",FACE,{"disambiguationData":[TD([[makeQuery(id+"F25.imprint","IMPRINT",EDGE,{"derivedFrom":sQuery(id+"F25.wireOp",EDGE,"E121.1.0")}),-1.0]])]});
            var Q2;
            Q2=makeQuery(id+"F24.imprint","IMPRINT",FACE,{"disambiguationData":[TD([[makeQuery(id+"F24.imprint","IMPRINT",EDGE,{"derivedFrom":sQuery(id+"F24.wireOp",EDGE,"E112")}),1.0]])]});
            loft(context, id + "F31", {"operationType" : NewBodyOperationType.ADD, "sheetProfilesArray" : [{ "sheetProfileEntities" : qUnion([Q1]) }, { "sheetProfileEntities" : qUnion([Q2]) }]});
        }
        {
            var Q0;
            Q0=makeQuery(id+"F21.imprint","IMPRINT",FACE,{"disambiguationData":[TD([[makeQuery(id+"F21.imprint","IMPRINT",EDGE,{"derivedFrom":sQuery(id+"F21.wireOp",EDGE,"E110")}),1.0]])]});
            extrude(context, id + "F32", {"entities" : qUnion([Q0]), "operationType" : NewBodyOperationType.ADD, "depth" : 20 * mm, "offsetDistance" : 25 * mm});
        }
        {
            var Q0;
            Q0=qCreatedBy(id+"F17.planeOp",FACE);
            cPlane(context, id + "F33", {"entities" : qUnion([Q0]), "cplaneType" : CPlaneType.OFFSET, "offset" : 2 * mm, "width" : 150 * mm, "height" : 150 * mm});
        }
        {
            var Q0;
            Q0=qCreatedBy(id+"F33.planeOp",FACE);
            var sketch = newSketch(context, id + "F34", { "sketchPlane" : qUnion([Q0])});
            skCircle(sketch, "E122", {"center": v(0, 0) * mm, "radius": 0.33 * mm});
            skCircle(sketch, "E123", {"center": v(0, 0) * mm, "radius": 4 * mm});
            skSolve(sketch);
        }
        {
            var Q0;
            Q0=makeQuery(id+"F34.imprint","IMPRINT",FACE,{"disambiguationData":[TD([[makeQuery(id+"F34.imprint","IMPRINT",EDGE,{"derivedFrom":sQuery(id+"F34.wireOp",EDGE,"E122")}),-1.0]])]});
            extrude(context, id + "F35", {"entities" : qUnion([Q0]), "depth" : 2 * mm, "offsetDistance" : 25 * mm});
        }
        {
            var Q0;
            Q0=qCreatedBy(id+"F33.planeOp",FACE);
            cPlane(context, id + "F36", {"entities" : qUnion([Q0]), "cplaneType" : CPlaneType.OFFSET, "offset" : 2.5 * mm, "width" : 150 * mm, "height" : 150 * mm});
        }
        {
            var Q0;
            Q0=qCreatedBy(id+"F36.planeOp",FACE);
            var sketch = newSketch(context, id + "F37", { "sketchPlane" : qUnion([Q0])});
            skCircle(sketch, "E124", {"center": v(0, 0) * mm, "radius": 4 * mm});
            skCircle(sketch, "E125", {"center": v(0, 0) * mm, "radius": 3.75 * mm});
            skLineSegment(sketch, "E126", {"start": v(-3.35, 1.03) * mm, "end": v(-3.58, 1.1) * mm});
            skLineSegment(sketch, "E127", {"start": v(-3, 1.81) * mm, "end": v(-3.2, 1.94) * mm});
            skArc(sketch, "E128", {"start": v(-3, 1.81) * mm, "mid": v(-3.2, 1.43) * mm, "end": v(-3.35, 1.03) * mm});
            skLineSegment(sketch, "E129.1.0", {"start": v(-3.07, -1.69) * mm, "end": v(-3.29, -1.8) * mm});
            skArc(sketch, "E129.1.1", {"start": v(-3.07, -1.69) * mm, "mid": v(-2.84, -2.05) * mm, "end": v(-2.56, -2.38) * mm});
            skLineSegment(sketch, "E129.1.2", {"start": v(-2.56, -2.38) * mm, "end": v(-2.75, -2.55) * mm});
            skLineSegment(sketch, "E129.2.0", {"start": v(-0.07, -3.5) * mm, "end": v(-0.08, -3.75) * mm});
            skArc(sketch, "E129.2.1", {"start": v(-0.07, -3.5) * mm, "mid": v(0.36, -3.48) * mm, "end": v(0.78, -3.41) * mm});
            skLineSegment(sketch, "E129.2.2", {"start": v(0.78, -3.41) * mm, "end": v(0.84, -3.65) * mm});
            skLineSegment(sketch, "E129.3.0", {"start": v(3, -1.81) * mm, "end": v(3.2, -1.94) * mm});
            skArc(sketch, "E129.3.1", {"start": v(3, -1.81) * mm, "mid": v(3.2, -1.43) * mm, "end": v(3.35, -1.03) * mm});
            skLineSegment(sketch, "E129.3.2", {"start": v(3.35, -1.03) * mm, "end": v(3.58, -1.1) * mm});
            skLineSegment(sketch, "E129.4.0", {"start": v(3.07, 1.69) * mm, "end": v(3.29, 1.8) * mm});
            skArc(sketch, "E129.4.1", {"start": v(3.07, 1.69) * mm, "mid": v(2.84, 2.05) * mm, "end": v(2.56, 2.38) * mm});
            skLineSegment(sketch, "E129.4.2", {"start": v(2.56, 2.38) * mm, "end": v(2.75, 2.55) * mm});
            skLineSegment(sketch, "E129.5.0", {"start": v(0.07, 3.5) * mm, "end": v(0.08, 3.75) * mm});
            skArc(sketch, "E129.5.1", {"start": v(0.07, 3.5) * mm, "mid": v(-0.36, 3.48) * mm, "end": v(-0.78, 3.41) * mm});
            skLineSegment(sketch, "E129.5.2", {"start": v(-0.78, 3.41) * mm, "end": v(-0.84, 3.65) * mm});
            skSolve(sketch);
        }
        {
            var Q0;
            Q0=makeQuery(id+"F37.imprint","IMPRINT",FACE,{"disambiguationData":[TD([[makeQuery(id+"F37.imprint","IMPRINT",EDGE,{"derivedFrom":sQuery(id+"F37.wireOp",EDGE,"E124")}),1.0]])]});
            extrude(context, id + "F38", {"entities" : qUnion([Q0]), "depth" : 4 * mm, "offsetDistance" : 25 * mm});
        }
        {
            var Q0;
            Q0=qCreatedBy(id+"F33.planeOp",FACE);
            cPlane(context, id + "F39", {"entities" : qUnion([Q0]), "cplaneType" : CPlaneType.OFFSET, "offset" : 2 * mm, "width" : 150 * mm, "height" : 150 * mm});
        }
        {
            var Q0;
            Q0=qCreatedBy(id+"F39.planeOp",FACE);
            var sketch = newSketch(context, id + "F40", { "sketchPlane" : qUnion([Q0])});
            skLineSegment(sketch, "E130", {"start": v(-1.04, 0.33) * mm, "end": v(-1.04, -0.33) * mm});
            skLineSegment(sketch, "E131", {"start": v(-1.04, 0.33) * mm, "end": v(-3.04, 0.33) * mm});
            skLineSegment(sketch, "E132", {"start": v(-3.04, 0.33) * mm, "end": v(-3.04, -0.33) * mm});
            skLineSegment(sketch, "E133", {"start": v(-3.04, -0.33) * mm, "end": v(-1.04, -0.33) * mm});
            skLineSegment(sketch, "E134.1.0", {"start": v(-0.8, -0.74) * mm, "end": v(-1.8, -2.47) * mm});
            skLineSegment(sketch, "E134.1.1", {"start": v(-1.8, -2.47) * mm, "end": v(-1.24, -2.8) * mm});
            skLineSegment(sketch, "E134.1.2", {"start": v(-1.24, -2.8) * mm, "end": v(-0.24, -1.06) * mm});
            skLineSegment(sketch, "E134.1.3", {"start": v(-0.8, -0.74) * mm, "end": v(-0.24, -1.06) * mm});
            skLineSegment(sketch, "E134.2.0", {"start": v(0.24, -1.06) * mm, "end": v(1.24, -2.8) * mm});
            skLineSegment(sketch, "E134.2.1", {"start": v(1.24, -2.8) * mm, "end": v(1.8, -2.47) * mm});
            skLineSegment(sketch, "E134.2.2", {"start": v(1.8, -2.47) * mm, "end": v(0.8, -0.74) * mm});
            skLineSegment(sketch, "E134.2.3", {"start": v(0.24, -1.06) * mm, "end": v(0.8, -0.74) * mm});
            skLineSegment(sketch, "E134.3.0", {"start": v(1.04, -0.33) * mm, "end": v(3.04, -0.33) * mm});
            skLineSegment(sketch, "E134.3.1", {"start": v(3.04, -0.33) * mm, "end": v(3.04, 0.33) * mm});
            skLineSegment(sketch, "E134.3.2", {"start": v(3.04, 0.33) * mm, "end": v(1.04, 0.33) * mm});
            skLineSegment(sketch, "E134.3.3", {"start": v(1.04, -0.33) * mm, "end": v(1.04, 0.33) * mm});
            skLineSegment(sketch, "E134.4.0", {"start": v(0.8, 0.74) * mm, "end": v(1.8, 2.47) * mm});
            skLineSegment(sketch, "E134.4.1", {"start": v(1.8, 2.47) * mm, "end": v(1.24, 2.8) * mm});
            skLineSegment(sketch, "E134.4.2", {"start": v(1.24, 2.8) * mm, "end": v(0.24, 1.06) * mm});
            skLineSegment(sketch, "E134.4.3", {"start": v(0.8, 0.74) * mm, "end": v(0.24, 1.06) * mm});
            skLineSegment(sketch, "E134.5.0", {"start": v(-0.24, 1.06) * mm, "end": v(-1.24, 2.8) * mm});
            skLineSegment(sketch, "E134.5.1", {"start": v(-1.24, 2.8) * mm, "end": v(-1.8, 2.47) * mm});
            skLineSegment(sketch, "E134.5.2", {"start": v(-1.8, 2.47) * mm, "end": v(-0.8, 0.74) * mm});
            skLineSegment(sketch, "E134.5.3", {"start": v(-0.24, 1.06) * mm, "end": v(-0.8, 0.74) * mm});
            skPoint(sketch, "E134.center", {"position": v(0, 0) * mm});
            skSolve(sketch);
        }
        {
            var Q0;
            Q0=makeQuery(id+"F40.imprint","IMPRINT",FACE,{"disambiguationData":[TD([[makeQuery(id+"F40.imprint","IMPRINT",EDGE,{"derivedFrom":sQuery(id+"F40.wireOp",EDGE,"E134.1.0")}),1.0]])]});
            var Q1;
            Q1=makeQuery(id+"F40.imprint","IMPRINT",FACE,{"disambiguationData":[TD([[makeQuery(id+"F40.imprint","IMPRINT",EDGE,{"derivedFrom":sQuery(id+"F40.wireOp",EDGE,"E130")}),-1.0]])]});
            var Q2;
            Q2=makeQuery(id+"F40.imprint","IMPRINT",FACE,{"disambiguationData":[TD([[makeQuery(id+"F40.imprint","IMPRINT",EDGE,{"derivedFrom":sQuery(id+"F40.wireOp",EDGE,"E134.5.0")}),1.0]])]});
            var Q3;
            Q3=makeQuery(id+"F40.imprint","IMPRINT",FACE,{"disambiguationData":[TD([[makeQuery(id+"F40.imprint","IMPRINT",EDGE,{"derivedFrom":sQuery(id+"F40.wireOp",EDGE,"E134.4.0")}),1.0]])]});
            var Q4;
            Q4=makeQuery(id+"F40.imprint","IMPRINT",FACE,{"disambiguationData":[TD([[makeQuery(id+"F40.imprint","IMPRINT",EDGE,{"derivedFrom":sQuery(id+"F40.wireOp",EDGE,"E134.3.0")}),1.0]])]});
            var Q5;
            Q5=makeQuery(id+"F40.imprint","IMPRINT",FACE,{"disambiguationData":[TD([[makeQuery(id+"F40.imprint","IMPRINT",EDGE,{"derivedFrom":sQuery(id+"F40.wireOp",EDGE,"E134.2.0")}),1.0]])]});
            extrude(context, id + "F41", {"entities" : qUnion([Q0, Q1, Q2, Q3, Q4, Q5]), "depth" : 4 * mm, "offsetDistance" : 25 * mm});
        }
        {
            var Q0;
            Q0=makeQuery(id+"F41.opExtrude","SWEPT_EDGE",EDGE,{"disambiguationData":[OSD([sQuery(id+"F40.wireOp",EDGE,"E132"),sQuery(id+"F40.wireOp",EDGE,"E133")])]});
            var Q1;
            Q1=makeQuery(id+"F41.opExtrude","SWEPT_EDGE",EDGE,{"disambiguationData":[OSD([sQuery(id+"F40.wireOp",EDGE,"E131"),sQuery(id+"F40.wireOp",EDGE,"E132")])]});
            var Q2;
            Q2=makeQuery(id+"F41.opExtrude","CAP_EDGE",EDGE,{"disambiguationData":[OSD([sQuery(id+"F40.wireOp",EDGE,"E132")])],"isStart":false});
            var Q3;
            Q3=makeQuery(id+"F41.opExtrude","CAP_EDGE",EDGE,{"disambiguationData":[OSD([sQuery(id+"F40.wireOp",EDGE,"E134.1.1")])],"isStart":false});
            var Q4;
            Q4=makeQuery(id+"F41.opExtrude","SWEPT_EDGE",EDGE,{"disambiguationData":[OSD([sQuery(id+"F40.wireOp",EDGE,"E134.1.0"),sQuery(id+"F40.wireOp",EDGE,"E134.1.1")])]});
            var Q5;
            Q5=makeQuery(id+"F41.opExtrude","SWEPT_EDGE",EDGE,{"disambiguationData":[OSD([sQuery(id+"F40.wireOp",EDGE,"E134.1.1"),sQuery(id+"F40.wireOp",EDGE,"E134.1.2")])]});
            var Q6;
            Q6=makeQuery(id+"F41.opExtrude","CAP_EDGE",EDGE,{"disambiguationData":[OSD([sQuery(id+"F40.wireOp",EDGE,"E134.2.1")])],"isStart":false});
            var Q7;
            Q7=makeQuery(id+"F41.opExtrude","SWEPT_EDGE",EDGE,{"disambiguationData":[OSD([sQuery(id+"F40.wireOp",EDGE,"E134.2.0"),sQuery(id+"F40.wireOp",EDGE,"E134.2.1")])]});
            var Q8;
            Q8=makeQuery(id+"F41.opExtrude","SWEPT_EDGE",EDGE,{"disambiguationData":[OSD([sQuery(id+"F40.wireOp",EDGE,"E134.2.1"),sQuery(id+"F40.wireOp",EDGE,"E134.2.2")])]});
            var Q9;
            Q9=makeQuery(id+"F41.opExtrude","CAP_EDGE",EDGE,{"disambiguationData":[OSD([sQuery(id+"F40.wireOp",EDGE,"E134.3.0")])],"isStart":false});
            var Q10;
            Q10=makeQuery(id+"F41.opExtrude","SWEPT_EDGE",EDGE,{"disambiguationData":[OSD([sQuery(id+"F40.wireOp",EDGE,"E134.3.0"),sQuery(id+"F40.wireOp",EDGE,"E134.3.1")])]});
            var Q11;
            Q11=makeQuery(id+"F41.opExtrude","SWEPT_EDGE",EDGE,{"disambiguationData":[OSD([sQuery(id+"F40.wireOp",EDGE,"E134.3.1"),sQuery(id+"F40.wireOp",EDGE,"E134.3.2")])]});
            var Q12;
            Q12=makeQuery(id+"F41.opExtrude","CAP_EDGE",EDGE,{"disambiguationData":[OSD([sQuery(id+"F40.wireOp",EDGE,"E134.3.1")])],"isStart":false});
            var Q13;
            Q13=makeQuery(id+"F41.opExtrude","CAP_EDGE",EDGE,{"disambiguationData":[OSD([sQuery(id+"F40.wireOp",EDGE,"E134.3.2")])],"isStart":false});
            var Q14;
            Q14=makeQuery(id+"F41.opExtrude","CAP_EDGE",EDGE,{"disambiguationData":[OSD([sQuery(id+"F40.wireOp",EDGE,"E134.2.0")])],"isStart":false});
            var Q15;
            Q15=makeQuery(id+"F41.opExtrude","CAP_EDGE",EDGE,{"disambiguationData":[OSD([sQuery(id+"F40.wireOp",EDGE,"E134.2.2")])],"isStart":false});
            var Q16;
            Q16=makeQuery(id+"F41.opExtrude","CAP_EDGE",EDGE,{"disambiguationData":[OSD([sQuery(id+"F40.wireOp",EDGE,"E134.1.2")])],"isStart":false});
            var Q17;
            Q17=makeQuery(id+"F41.opExtrude","CAP_EDGE",EDGE,{"disambiguationData":[OSD([sQuery(id+"F40.wireOp",EDGE,"E134.1.0")])],"isStart":false});
            var Q18;
            Q18=makeQuery(id+"F41.opExtrude","SWEPT_EDGE",EDGE,{"disambiguationData":[OSD([sQuery(id+"F40.wireOp",EDGE,"E134.5.1"),sQuery(id+"F40.wireOp",EDGE,"E134.5.2")])]});
            var Q19;
            Q19=makeQuery(id+"F41.opExtrude","SWEPT_EDGE",EDGE,{"disambiguationData":[OSD([sQuery(id+"F40.wireOp",EDGE,"E134.5.0"),sQuery(id+"F40.wireOp",EDGE,"E134.5.1")])]});
            var Q20;
            Q20=makeQuery(id+"F41.opExtrude","CAP_EDGE",EDGE,{"disambiguationData":[OSD([sQuery(id+"F40.wireOp",EDGE,"E134.5.1")])],"isStart":false});
            var Q21;
            Q21=makeQuery(id+"F41.opExtrude","CAP_EDGE",EDGE,{"disambiguationData":[OSD([sQuery(id+"F40.wireOp",EDGE,"E134.5.2")])],"isStart":false});
            var Q22;
            Q22=makeQuery(id+"F41.opExtrude","CAP_FACE",FACE,{"disambiguationData":[OSD([sQuery(id+"F40.wireOp",EDGE,"E134.5.0"),sQuery(id+"F40.wireOp",EDGE,"E134.5.1"),sQuery(id+"F40.wireOp",EDGE,"E134.5.2"),sQuery(id+"F40.wireOp",EDGE,"E134.5.3")])],"isStart":false});
            var Q23;
            Q23=makeQuery(id+"F41.opExtrude","CAP_EDGE",EDGE,{"disambiguationData":[OSD([sQuery(id+"F40.wireOp",EDGE,"E134.4.2")])],"isStart":false});
            var Q24;
            Q24=makeQuery(id+"F41.opExtrude","CAP_EDGE",EDGE,{"disambiguationData":[OSD([sQuery(id+"F40.wireOp",EDGE,"E134.4.0")])],"isStart":false});
            var Q25;
            Q25=makeQuery(id+"F41.opExtrude","CAP_EDGE",EDGE,{"disambiguationData":[OSD([sQuery(id+"F40.wireOp",EDGE,"E134.4.1")])],"isStart":false});
            var Q26;
            Q26=makeQuery(id+"F41.opExtrude","SWEPT_EDGE",EDGE,{"disambiguationData":[OSD([sQuery(id+"F40.wireOp",EDGE,"E134.4.1"),sQuery(id+"F40.wireOp",EDGE,"E134.4.2")])]});
            var Q27;
            Q27=makeQuery(id+"F41.opExtrude","SWEPT_EDGE",EDGE,{"disambiguationData":[OSD([sQuery(id+"F40.wireOp",EDGE,"E134.4.0"),sQuery(id+"F40.wireOp",EDGE,"E134.4.1")])]});
            fillet(context, id + "F42", {"entities" : qUnion([Q0, Q1, Q2, Q3, Q4, Q5, Q6, Q7, Q8, Q9, Q10, Q11, Q12, Q13, Q14, Q15, Q16, Q17, Q18, Q19, Q20, Q21, Q22, Q23, Q24, Q25, Q26, Q27]), "radius" : 0.2 * mm, "tangentPropagation" : true, "allowEdgeOverflow" : false});
        }
        {
            var Q0;
            {var subQ0=sQuery(id+"F37.wireOp",EDGE,"E126");Q0=makeQuery(id+"F37.imprint","IMPRINT",FACE,{"disambiguationData":[TD([[makeQuery(id+"F37.imprint","IMPRINT",EDGE,{"derivedFrom":subQ0}),-1.0]])]});}
            var Q1;
            {var subQ0=sQuery(id+"F37.wireOp",EDGE,"E129.5.0");Q1=makeQuery(id+"F37.imprint","IMPRINT",FACE,{"disambiguationData":[TD([[makeQuery(id+"F37.imprint","IMPRINT",EDGE,{"derivedFrom":subQ0}),1.0]])]});}
            var Q2;
            {var subQ0=sQuery(id+"F37.wireOp",EDGE,"E129.4.0");Q2=makeQuery(id+"F37.imprint","IMPRINT",FACE,{"disambiguationData":[TD([[makeQuery(id+"F37.imprint","IMPRINT",EDGE,{"derivedFrom":subQ0}),1.0]])]});}
            var Q3;
            {var subQ0=sQuery(id+"F37.wireOp",EDGE,"E129.3.0");Q3=makeQuery(id+"F37.imprint","IMPRINT",FACE,{"disambiguationData":[TD([[makeQuery(id+"F37.imprint","IMPRINT",EDGE,{"derivedFrom":subQ0}),1.0]])]});}
            var Q4;
            {var subQ0=sQuery(id+"F37.wireOp",EDGE,"E129.2.0");Q4=makeQuery(id+"F37.imprint","IMPRINT",FACE,{"disambiguationData":[TD([[makeQuery(id+"F37.imprint","IMPRINT",EDGE,{"derivedFrom":subQ0}),1.0]])]});}
            var Q5;
            {var subQ0=sQuery(id+"F37.wireOp",EDGE,"E129.1.0");Q5=makeQuery(id+"F37.imprint","IMPRINT",FACE,{"disambiguationData":[TD([[makeQuery(id+"F37.imprint","IMPRINT",EDGE,{"derivedFrom":subQ0}),1.0]])]});}
            extrude(context, id + "F43", {"entities" : qUnion([Q0, Q1, Q2, Q3, Q4, Q5]), "depth" : 4 * mm, "offsetDistance" : 25 * mm});
        }
        {
            var Q0;
            Q0=qCreatedBy(id+"F36.planeOp",FACE);
            cPlane(context, id + "F44", {"entities" : qUnion([Q0]), "cplaneType" : CPlaneType.OFFSET, "offset" : 4 * mm, "width" : 150 * mm, "height" : 150 * mm});
        }
        {
            var Q0;
            Q0=qCreatedBy(id+"F44.planeOp",FACE);
            var sketch = newSketch(context, id + "F45", { "sketchPlane" : qUnion([Q0])});
            skCircle(sketch, "E135", {"center": v(0, 0) * mm, "radius": 0.33 * mm});
            skCircle(sketch, "E136", {"center": v(0, 0) * mm, "radius": 1.4 * mm});
            skCircle(sketch, "E137", {"center": v(0, 0) * mm, "radius": 4 * mm});
            skCircle(sketch, "E138", {"center": v(0, 0) * mm, "radius": 3.75 * mm});
            skLineSegment(sketch, "E139.trimOffspring", {"start": v(-1.16, 0.78) * mm, "end": v(-3.11, 2.09) * mm});
            skLineSegment(sketch, "E140.trimOffspring", {"start": v(-1.4, 0) * mm, "end": v(-3.75, 0) * mm});
            skLineSegment(sketch, "E141.1.0", {"start": v(-0.1, -1.4) * mm, "end": v(-0.25, -3.74) * mm});
            skLineSegment(sketch, "E141.1.1", {"start": v(0.7, -1.21) * mm, "end": v(1.88, -3.25) * mm});
            skLineSegment(sketch, "E141.2.0", {"start": v(1.26, 0.62) * mm, "end": v(3.37, 1.65) * mm});
            skLineSegment(sketch, "E141.2.1", {"start": v(0.7, 1.21) * mm, "end": v(1.88, 3.25) * mm});
            skSolve(sketch);
        }
        {
            var Q0;
            {var subQ0=sQuery(id+"F45.wireOp",EDGE,"E139.trimOffspring");Q0=makeQuery(id+"F45.imprint","IMPRINT",FACE,{"disambiguationData":[TD([[makeQuery(id+"F45.imprint","IMPRINT",EDGE,{"derivedFrom":subQ0}),1.0]])]});}
            var Q1;
            {var subQ0=sQuery(id+"F45.wireOp",EDGE,"E141.2.0");Q1=makeQuery(id+"F45.imprint","IMPRINT",FACE,{"disambiguationData":[TD([[makeQuery(id+"F45.imprint","IMPRINT",EDGE,{"derivedFrom":subQ0}),1.0]])]});}
            var Q2;
            {var subQ0=sQuery(id+"F45.wireOp",EDGE,"E141.1.0");Q2=makeQuery(id+"F45.imprint","IMPRINT",FACE,{"disambiguationData":[TD([[makeQuery(id+"F45.imprint","IMPRINT",EDGE,{"derivedFrom":subQ0}),1.0]])]});}
            var Q3;
            Q3=makeQuery(id+"F45.imprint","IMPRINT",FACE,{"disambiguationData":[TD([[makeQuery(id+"F45.imprint","IMPRINT",EDGE,{"derivedFrom":sQuery(id+"F45.wireOp",EDGE,"E135")}),-1.0]])]});
            var Q4;
            Q4=makeQuery(id+"F45.imprint","IMPRINT",FACE,{"disambiguationData":[TD([[makeQuery(id+"F45.imprint","IMPRINT",EDGE,{"derivedFrom":sQuery(id+"F45.wireOp",EDGE,"E137")}),1.0]])]});
            extrude(context, id + "F46", {"entities" : qUnion([Q0, Q1, Q2, Q3, Q4]), "operationType" : NewBodyOperationType.ADD, "depth" : 0.5 * mm, "offsetDistance" : 25 * mm});
        }
        {
            var Q0;
            Q0=makeQuery(id+"F46.opExtrude","CAP_EDGE",EDGE,{"disambiguationData":[OSD([sQuery(id+"F45.wireOp",EDGE,"E137")])],"isStart":false});
            fillet(context, id + "F47", {"entities" : qUnion([Q0]), "radius" : 0.2 * mm, "tangentPropagation" : true, "allowEdgeOverflow" : false});
        }
        {
            var Q0;
            Q0=makeQuery(id+"F31.boolean.opBoolean","MERGE",FACE,{"derivedFrom":[makeQuery(id+"F30.boolean.opBoolean","MERGE",FACE,{"derivedFrom":[makeQuery(id+"F29.boolean.opBoolean","MERGE",FACE,{"derivedFrom":[makeQuery(id+"F28.boolean.opBoolean","MERGE",FACE,{"derivedFrom":[makeQuery(id+"F27.boolean.opBoolean","MERGE",FACE,{"derivedFrom":[makeQuery(id+"F26.boolean.opBoolean","MERGE",FACE,{"derivedFrom":[makeQuery(id+"F22.opExtrude","CAP_FACE",FACE,{"disambiguationData":[OSD([sQuery(id+"F21.wireOp",EDGE,"E108"),sQuery(id+"F21.wireOp",EDGE,"E110")])],"isStart":true}),makeQuery(id+"F26.opLoft","CAP_FACE",FACE,{"disambiguationData":[OSD([makeQuery(id+"F25.imprint","IMPRINT",FACE,{"disambiguationData":[TD([[makeQuery(id+"F25.imprint","IMPRINT",EDGE,{"derivedFrom":sQuery(id+"F25.wireOp",EDGE,"E121.2.0")}),-1.0]])]})])],"isStart":true})]}),makeQuery(id+"F27.opLoft","CAP_FACE",FACE,{"disambiguationData":[OSD([makeQuery(id+"F25.imprint","IMPRINT",FACE,{"disambiguationData":[TD([[makeQuery(id+"F25.imprint","IMPRINT",EDGE,{"derivedFrom":sQuery(id+"F25.wireOp",EDGE,"E121.3.0")}),-1.0]])]})])],"isStart":true})]}),makeQuery(id+"F28.opLoft","CAP_FACE",FACE,{"disambiguationData":[OSD([makeQuery(id+"F25.imprint","IMPRINT",FACE,{"disambiguationData":[TD([[makeQuery(id+"F25.imprint","IMPRINT",EDGE,{"derivedFrom":sQuery(id+"F25.wireOp",EDGE,"E121.4.0")}),-1.0]])]})])],"isStart":true})]}),makeQuery(id+"F29.opLoft","CAP_FACE",FACE,{"disambiguationData":[OSD([makeQuery(id+"F25.imprint","IMPRINT",FACE,{"disambiguationData":[TD([[makeQuery(id+"F25.imprint","IMPRINT",EDGE,{"derivedFrom":sQuery(id+"F25.wireOp",EDGE,"E121.5.0")}),-1.0]])]})])],"isStart":true})]}),makeQuery(id+"F30.opLoft","CAP_FACE",FACE,{"disambiguationData":[OSD([makeQuery(id+"F25.imprint","IMPRINT",FACE,{"disambiguationData":[TD([[makeQuery(id+"F25.imprint","IMPRINT",EDGE,{"derivedFrom":sQuery(id+"F25.wireOp",EDGE,"E117")}),-1.0]])]})])],"isStart":true})]}),makeQuery(id+"F31.opLoft","CAP_FACE",FACE,{"disambiguationData":[OSD([makeQuery(id+"F25.imprint","IMPRINT",FACE,{"disambiguationData":[TD([[makeQuery(id+"F25.imprint","IMPRINT",EDGE,{"derivedFrom":sQuery(id+"F25.wireOp",EDGE,"E121.1.0")}),-1.0]])]})])],"isStart":true})]});
            var sketch = newSketch(context, id + "F48", { "sketchPlane" : qUnion([Q0])});
            skCircle(sketch, "E142", {"center": v(0, 0) * mm, "radius": 2.5 * mm});
            skSolve(sketch);
        }
        {
            var Q0;
            Q0=makeQuery(id+"F48.imprint","IMPRINT",FACE,{"disambiguationData":[TD([[makeQuery(id+"F48.imprint","IMPRINT",EDGE,{"derivedFrom":sQuery(id+"F48.wireOp",EDGE,"E142")}),1.0]])]});
            extrude(context, id + "F49", {"entities" : qUnion([Q0]), "operationType" : NewBodyOperationType.ADD, "depth" : 10 * mm, "offsetDistance" : 25 * mm});
        }
    });
